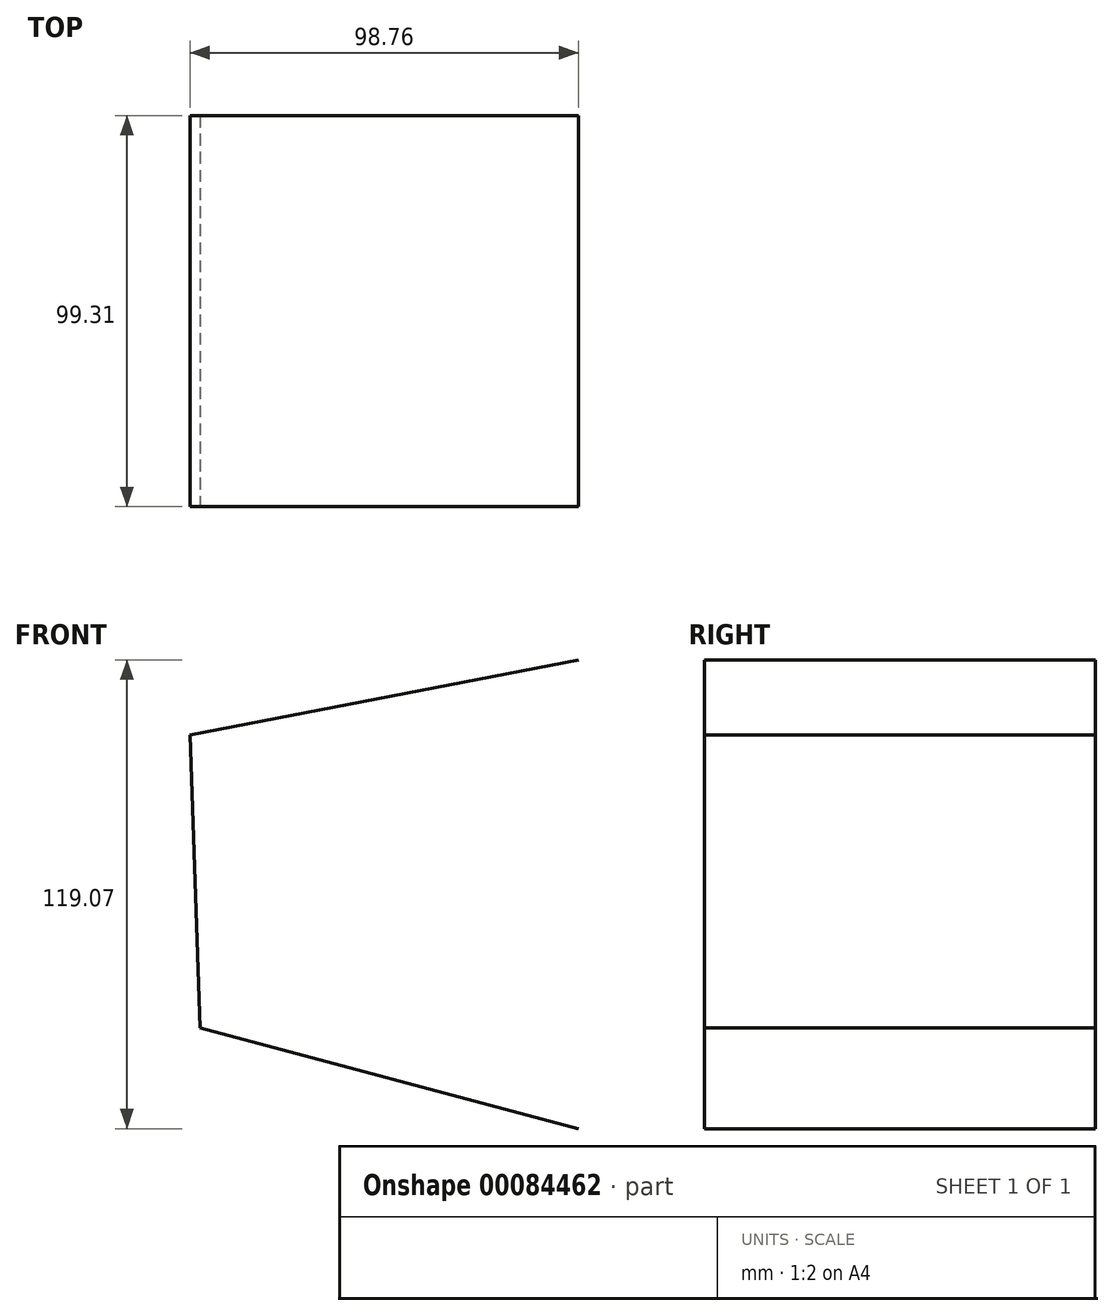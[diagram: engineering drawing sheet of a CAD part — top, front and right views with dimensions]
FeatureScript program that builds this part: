
annotation { "Feature Type Name" : "Feature", "Feature Type Description" : "" }
export const myFeature = defineFeature(function(context is Context, id is Id, definition is map)
    precondition{}
    {
        {
            var Q0;
            Q0=qCreatedBy(makeId("Front.planeOp"),FACE);
            var sketch = newSketch(context, id + "F0", { "sketchPlane" : qUnion([Q0])});
            skLineSegment(sketch, "E0", {"start": v(-50.86, 38.68) * mm, "end": v(47.9, 57.77) * mm});
            skLineSegment(sketch, "E1", {"start": v(47.9, -61.3) * mm, "end": v(-48.23, -35.72) * mm});
            skLineSegment(sketch, "E2", {"start": v(-48.23, -35.72) * mm, "end": v(-50.86, 38.68) * mm});
            skFitSpline(sketch, "E3", {"points": [v(-12.67, 13.66) * mm, v(61.72, 20.24) * mm, v(69.62, 65.01) * mm, v(37.36, 72.91) * mm, v(-63.37, 53.16) * mm, v(-68.64, -48.88) * mm, v(57.77, -87.07) * mm, v(72.26, -31.77) * mm, v(-15.97, -15.3) * mm, v(-12.67, 13.66) * mm]});
            skFitSpline(sketch, "E4", {"points": [v(-110.77, 51.19) * mm, v(-118.21, 28.27) * mm, v(-147.18, 0) * mm, v(-180.85, -39.85) * mm, v(-105.5, -71.27) * mm, v(-129.86, -98.26) * mm, v(-219.4, -37.7) * mm, v(-142.37, 49.21) * mm, v(-129.86, 61.06) * mm], "startDerivative": vector(379.04, -246.37) * mm, "endDerivative": vector(498.38, -146.58) * mm});
            skSolve(sketch);
        }
        {
            var Q0;
            Q0=sQuery(id+"F0.wireOp",EDGE,"E0");
            var Q1;
            Q1=sQuery(id+"F0.wireOp",EDGE,"E2");
            var Q2;
            Q2=sQuery(id+"F0.wireOp",EDGE,"E1");
            extrude(context, id + "F1", {"bodyType" : ToolBodyType.SURFACE, "surfaceEntities" : qUnion([Q0, Q1, Q2]), "depth" : 99.31 * mm});
        }
    });
